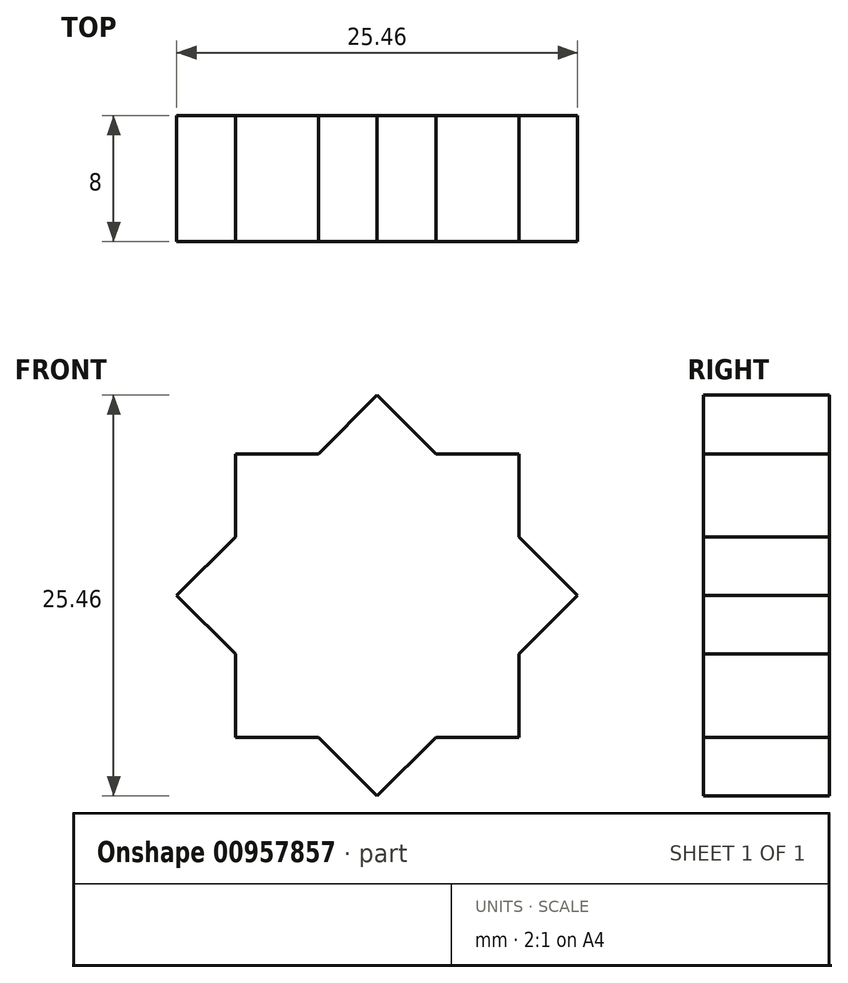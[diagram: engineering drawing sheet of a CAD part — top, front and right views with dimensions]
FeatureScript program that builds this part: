
annotation { "Feature Type Name" : "Feature", "Feature Type Description" : "" }
export const myFeature = defineFeature(function(context is Context, id is Id, definition is map)
    precondition{}
    {
        {
            var Q0;
            Q0=qCreatedBy(makeId("Front.planeOp"),FACE);
            var sketch = newSketch(context, id + "F0", { "sketchPlane" : qUnion([Q0])});
            skLineSegment(sketch, "E0", {"start": v(-12.73, 0) * mm, "end": v(0, 12.73) * mm});
            skLineSegment(sketch, "E1", {"start": v(0, 12.73) * mm, "end": v(12.73, 0) * mm});
            skLineSegment(sketch, "E2", {"start": v(12.73, 0) * mm, "end": v(0, -12.73) * mm});
            skLineSegment(sketch, "E3", {"start": v(0, -12.73) * mm, "end": v(-12.73, 0) * mm});
            skSolve(sketch);
        }
        {
            var Q0;
            Q0=makeQuery(id+"F0.imprint","IMPRINT",FACE,{"disambiguationData":[TD([[makeQuery(id+"F0.imprint","IMPRINT",EDGE,{"derivedFrom":sQuery(id+"F0.wireOp",EDGE,"E0")}),-1.0]])]});
            var sketch = newSketch(context, id + "F1", { "sketchPlane" : qUnion([Q0])});
            skLineSegment(sketch, "E4.bottom", {"start": v(9, 9) * mm, "end": v(-9, 9) * mm});
            skLineSegment(sketch, "E4.top", {"start": v(9, -9) * mm, "end": v(-9, -9) * mm});
            skLineSegment(sketch, "E4.left", {"start": v(9, 9) * mm, "end": v(9, -9) * mm});
            skLineSegment(sketch, "E4.right", {"start": v(-9, 9) * mm, "end": v(-9, -9) * mm});
            skPoint(sketch, "E4.middle", {"position": v(0, 0) * mm});
            skSolve(sketch);
        }
        {
            var Q0;
            {var subQ0=sQuery(id+"F1.wireOp",EDGE,"E4.right");var subQ1=sQuery(id+"F1.wireOp",EDGE,"E4.bottom");var subQ2=makeQuery(id+"F1.imprint","INTERSECT",VERTEX,{"derivedFrom":[subQ1,subQ0]});Q0=makeQuery(id+"F1.imprint","IMPRINT",FACE,{"disambiguationData":[TD([[makeQuery(id+"F1.imprint","IMPRINT",EDGE,{"disambiguationData":[TD([[subQ2,1.0]])],"derivedFrom":subQ1}),1.0]])]});}
            var Q1;
            {var subQ0=sQuery(id+"F1.wireOp",EDGE,"E4.left");var subQ1=sQuery(id+"F1.wireOp",EDGE,"E4.bottom");var subQ2=makeQuery(id+"F1.imprint","INTERSECT",VERTEX,{"derivedFrom":[subQ1,subQ0]});Q1=makeQuery(id+"F1.imprint","IMPRINT",FACE,{"disambiguationData":[TD([[makeQuery(id+"F1.imprint","IMPRINT",EDGE,{"disambiguationData":[TD([[subQ2,-1.0]])],"derivedFrom":subQ1}),1.0]])]});}
            var Q2;
            {var subQ0=sQuery(id+"F1.wireOp",EDGE,"E4.bottom");var subQ1=makeQuery(id+"F0.imprint","IMPRINT",EDGE,{"derivedFrom":sQuery(id+"F0.wireOp",EDGE,"E1")});var subQ2=makeQuery(id+"F1.imprint","INTERSECT",VERTEX,{"derivedFrom":[subQ1,subQ0]});Q2=makeQuery(id+"F1.imprint","IMPRINT",FACE,{"disambiguationData":[TD([[makeQuery(id+"F1.imprint","IMPRINT",EDGE,{"disambiguationData":[TD([[subQ2,-1.0]])],"derivedFrom":subQ0}),-1.0]])]});}
            var Q3;
            {var subQ0=sQuery(id+"F1.wireOp",EDGE,"E4.right");var subQ1=makeQuery(id+"F0.imprint","IMPRINT",EDGE,{"derivedFrom":sQuery(id+"F0.wireOp",EDGE,"E0")});var subQ2=makeQuery(id+"F1.imprint","INTERSECT",VERTEX,{"derivedFrom":[subQ1,subQ0]});Q3=makeQuery(id+"F1.imprint","IMPRINT",FACE,{"disambiguationData":[TD([[makeQuery(id+"F1.imprint","IMPRINT",EDGE,{"disambiguationData":[TD([[subQ2,-1.0]])],"derivedFrom":subQ0}),-1.0]])]});}
            var Q4;
            {var subQ0=sQuery(id+"F1.wireOp",EDGE,"E4.right");var subQ1=sQuery(id+"F1.wireOp",EDGE,"E4.top");var subQ2=makeQuery(id+"F1.imprint","INTERSECT",VERTEX,{"derivedFrom":[subQ1,subQ0]});Q4=makeQuery(id+"F1.imprint","IMPRINT",FACE,{"disambiguationData":[TD([[makeQuery(id+"F1.imprint","IMPRINT",EDGE,{"disambiguationData":[TD([[subQ2,1.0]])],"derivedFrom":subQ1}),-1.0]])]});}
            var Q5;
            {var subQ0=sQuery(id+"F1.wireOp",EDGE,"E4.top");var subQ1=makeQuery(id+"F0.imprint","IMPRINT",EDGE,{"derivedFrom":sQuery(id+"F0.wireOp",EDGE,"E2")});var subQ2=makeQuery(id+"F1.imprint","INTERSECT",VERTEX,{"derivedFrom":[subQ1,subQ0]});Q5=makeQuery(id+"F1.imprint","IMPRINT",FACE,{"disambiguationData":[TD([[makeQuery(id+"F1.imprint","IMPRINT",EDGE,{"disambiguationData":[TD([[subQ2,-1.0]])],"derivedFrom":subQ0}),1.0]])]});}
            var Q6;
            {var subQ0=sQuery(id+"F1.wireOp",EDGE,"E4.left");var subQ1=sQuery(id+"F1.wireOp",EDGE,"E4.top");var subQ2=makeQuery(id+"F1.imprint","INTERSECT",VERTEX,{"derivedFrom":[subQ1,subQ0]});Q6=makeQuery(id+"F1.imprint","IMPRINT",FACE,{"disambiguationData":[TD([[makeQuery(id+"F1.imprint","IMPRINT",EDGE,{"disambiguationData":[TD([[subQ2,-1.0]])],"derivedFrom":subQ1}),-1.0]])]});}
            var Q7;
            {var subQ0=sQuery(id+"F1.wireOp",EDGE,"E4.left");var subQ1=makeQuery(id+"F0.imprint","IMPRINT",EDGE,{"derivedFrom":sQuery(id+"F0.wireOp",EDGE,"E1")});var subQ2=makeQuery(id+"F1.imprint","INTERSECT",VERTEX,{"derivedFrom":[subQ1,subQ0]});Q7=makeQuery(id+"F1.imprint","IMPRINT",FACE,{"disambiguationData":[TD([[makeQuery(id+"F1.imprint","IMPRINT",EDGE,{"disambiguationData":[TD([[subQ2,-1.0]])],"derivedFrom":subQ0}),1.0]])]});}
            var Q8;
            {var subQ6=makeQuery(id+"F0.imprint","IMPRINT",EDGE,{"derivedFrom":sQuery(id+"F0.wireOp",EDGE,"E1")});var subQ13=sQuery(id+"F1.wireOp",EDGE,"E4.bottom");var subQ14=makeQuery(id+"F1.imprint","INTERSECT",VERTEX,{"derivedFrom":[subQ6,subQ13]});Q8=makeQuery(id+"F1.imprint","IMPRINT",FACE,{"disambiguationData":[TD([[makeQuery(id+"F1.imprint","IMPRINT",EDGE,{"disambiguationData":[TD([[subQ14,-1.0]])],"derivedFrom":subQ13}),1.0]])]});}
            extrude(context, id + "F2", {"entities" : qUnion([Q0, Q1, Q2, Q3, Q4, Q5, Q6, Q7, Q8]), "depth" : 8 * mm, "offsetDistance" : 25 * mm});
        }
    });
